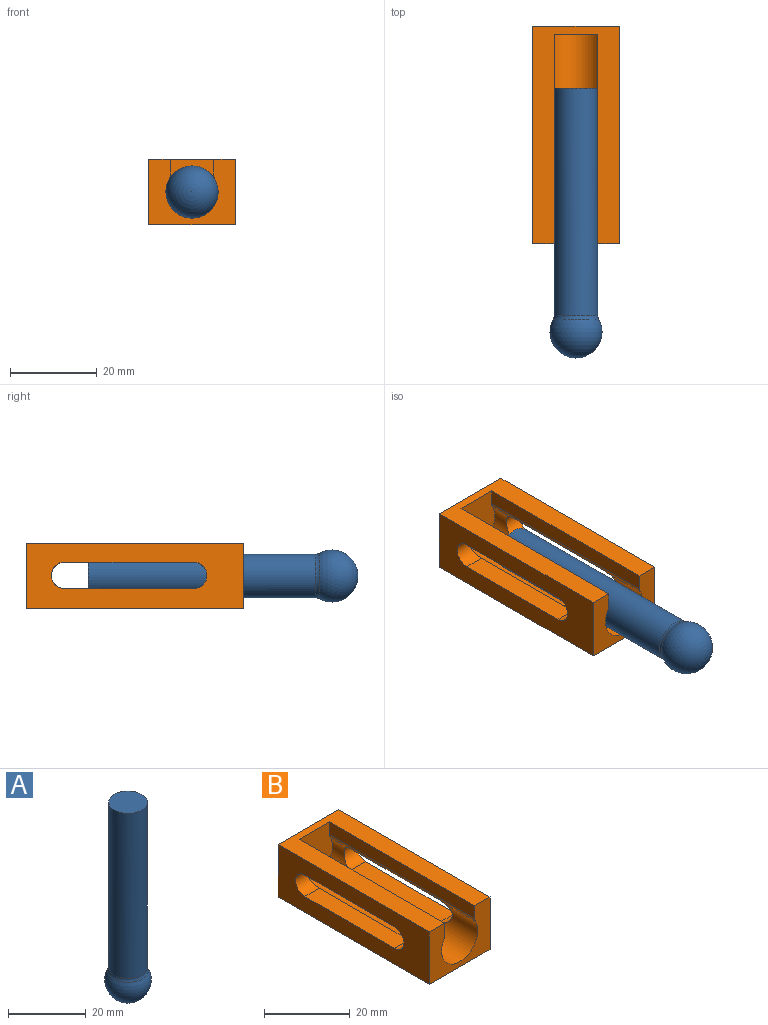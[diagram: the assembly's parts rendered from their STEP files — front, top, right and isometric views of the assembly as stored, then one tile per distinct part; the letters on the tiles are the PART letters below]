
ASSEMBLY  parts=2 mates=1
PART A: 4 faces, bbox 12.1x12.1x62 mm
  f0: sphere r=6mm, area 335.7mm2, adj f3
  f1: cylinder r=5mm len=52.13mm, axis (0,0,1), area 1637.6mm2, adj f2,f3
  f2: plane 10x10mm, normal (0,0,1), area 78.5mm2, adj f1
  f3: torus R=7mm, axis (0,0,-1), area 32.3mm2, adj f0,f1
PART B: 20 faces, bbox 20x50x15 mm
  f0: plane 50x20mm, normal (0,0,-1), area 1000mm2, adj f1,f6,f7,f8
  f1: plane 50x15mm, normal (1,0,0), area 539.4mm2, adj f0,f2,f7,f8,f14,f15,f16,f17
  f2: plane 50x20mm, normal (0,0,1), area 520mm2, adj f1,f3,f5,f6,f7,f8,f9
  f3: plane 48x3.63mm, normal (-1,0,0), area 174.1mm2, adj f2,f7,f9,f19
  f4: cylinder r=6mm len=48mm, axis (0,1,0), area 775.2mm2, adj f7,f9,f11,f12,f13,f14,f15,f16
  f5: plane 48x3.63mm, normal (1,0,0), area 174.1mm2, adj f2,f7,f9,f18
  f6: plane 50x15mm, normal (-1,0,0), area 539.4mm2, adj f0,f2,f7,f8,f10,f11,f12,f13
  f7: plane 20x15mm, normal (0,-1,0), area 163.9mm2, adj f0,f1,f2,f3,f4,f5,f6,f18
  f8: plane 20x15mm, normal (0,1,0), area 300mm2, adj f0,f1,f2,f6
  f9: plane 13.5x12mm, normal (0,-1,0), area 136.1mm2, adj f2,f3,f4,f5,f18,f19
  f10: plane 29.64x4.88mm, normal (0,0,-1), area 144.6mm2, adj f6,f11,f13,f18
  f11: cylinder r=3.06mm len=6.11mm, axis (-1,0,0), area 42.3mm2, adj f4,f6,f10,f12,f18
  f12: plane 29.64x4.76mm, normal (0,0,1), area 141.2mm2, adj f4,f6,f11,f13
  f13: cylinder r=3.06mm len=6.11mm, axis (-1,0,0), area 42.3mm2, adj f4,f6,f10,f12,f18
  f14: cylinder r=3.06mm len=6.11mm, axis (-1,0,0), area 42.3mm2, adj f1,f4,f15,f17,f19
  f15: plane 29.64x4.76mm, normal (0,0,1), area 141.2mm2, adj f1,f4,f14,f16
  f16: cylinder r=3.06mm len=6.11mm, axis (-1,0,0), area 42.3mm2, adj f1,f4,f15,f17,f19
  f17: plane 29.64x4.88mm, normal (0,0,-1), area 144.6mm2, adj f1,f14,f16,f19
  f18: cylinder r=2mm len=48mm, axis (0,1,0), area 38.7mm2, adj f4,f5,f7,f9,f10,f11,f13
  f19: cylinder r=2mm len=48mm, axis (0,1,0), area 38.7mm2, adj f3,f4,f7,f9,f14,f16,f17
PLACE A rot(axis=(-0.02,-0.71,-0.71),177.6deg) t=(0,-70.32,7.5)mm
PLACE B at identity fixed
MATE cylindrical A.f1 <-> B.f4  axis (0,1,0) through (0,-40.38,7.5)mm
